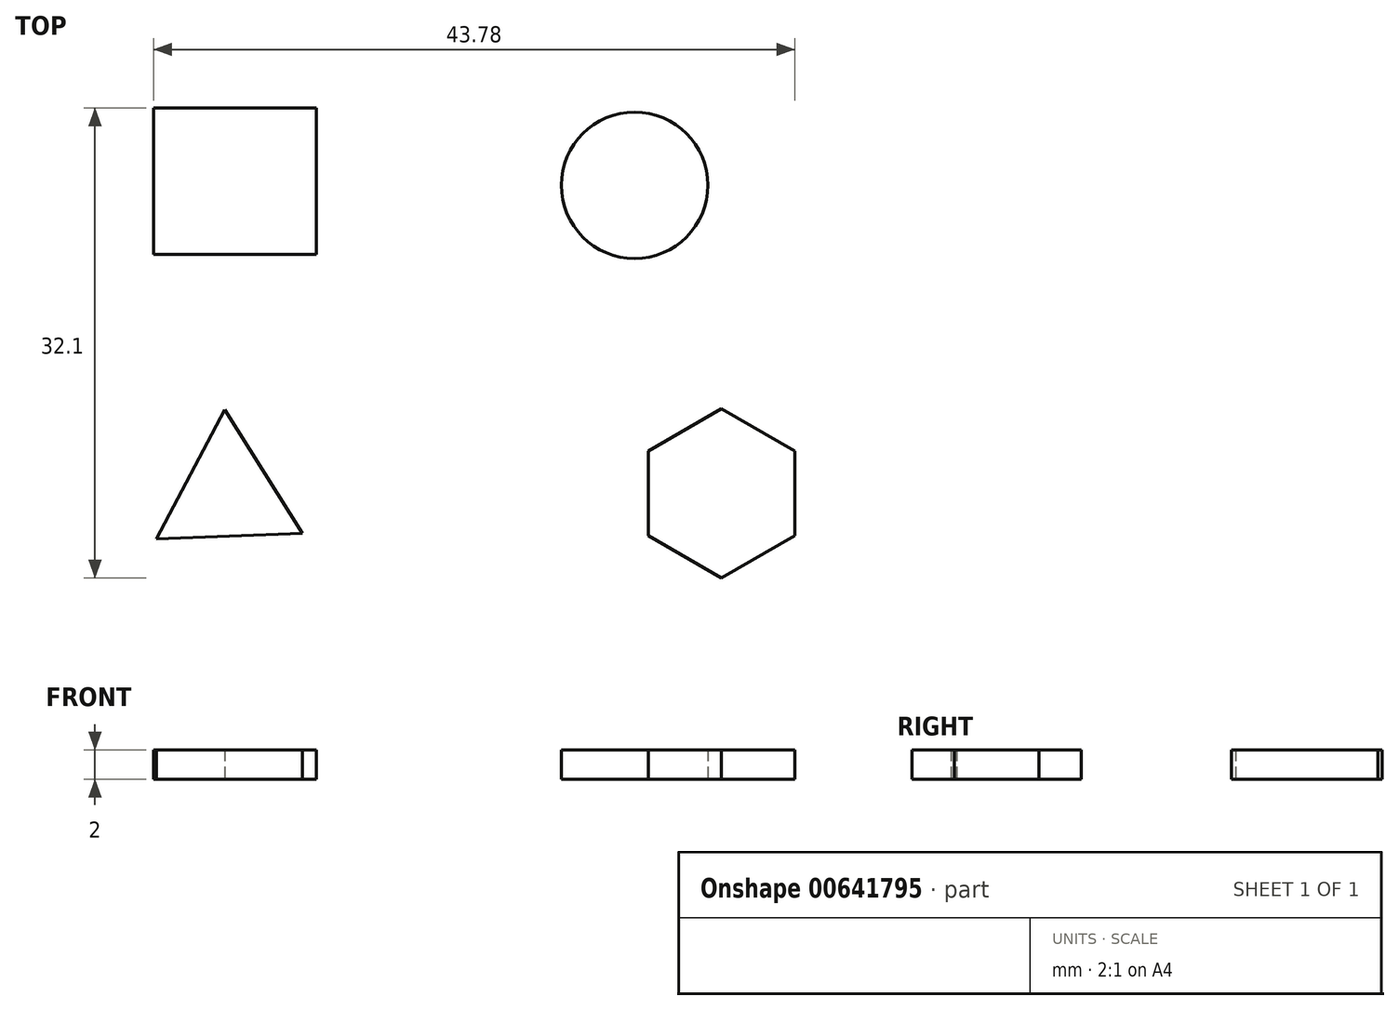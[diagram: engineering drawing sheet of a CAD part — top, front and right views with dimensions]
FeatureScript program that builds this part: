
annotation { "Feature Type Name" : "Feature", "Feature Type Description" : "" }
export const myFeature = defineFeature(function(context is Context, id is Id, definition is map)
    precondition{}
    {
        {
            var Q0;
            Q0=qCreatedBy(makeId("Top.planeOp"),FACE);
            var sketch = newSketch(context, id + "F0", { "sketchPlane" : qUnion([Q0])});
            skCircle(sketch, "E0", {"center": v(7.96, 9.92) * mm, "radius": 5 * mm});
            skLineSegment(sketch, "E1.bottom", {"start": v(-13.78, 15.2) * mm, "end": v(-24.88, 15.2) * mm});
            skLineSegment(sketch, "E1.top", {"start": v(-13.78, 5.2) * mm, "end": v(-24.88, 5.2) * mm});
            skLineSegment(sketch, "E1.left", {"start": v(-13.78, 15.2) * mm, "end": v(-13.78, 5.2) * mm});
            skLineSegment(sketch, "E1.right", {"start": v(-24.88, 15.2) * mm, "end": v(-24.88, 5.2) * mm});
            skPoint(sketch, "E1.middle", {"position": v(-19.33, 10.2) * mm});
            skLineSegment(sketch, "E2", {"start": v(-24.7, -14.23) * mm, "end": v(-20.02, -5.4) * mm});
            skLineSegment(sketch, "E3", {"start": v(-20.02, -5.4) * mm, "end": v(-14.7, -13.86) * mm});
            skLineSegment(sketch, "E4", {"start": v(-14.7, -13.86) * mm, "end": v(-24.7, -14.23) * mm});
            skCircle(sketch, "E5.cCircle", {"center": v(13.9, -11.13) * mm, "radius": 5 * mm, "construction": true});
            skLineSegment(sketch, "E5.0", {"start": v(18.9, -8.24) * mm, "end": v(18.9, -14.01) * mm});
            skLineSegment(sketch, "E5.1", {"start": v(18.9, -14.01) * mm, "end": v(13.9, -16.9) * mm});
            skLineSegment(sketch, "E5.2", {"start": v(13.9, -16.9) * mm, "end": v(8.9, -14.01) * mm});
            skLineSegment(sketch, "E5.3", {"start": v(8.9, -14.01) * mm, "end": v(8.9, -8.24) * mm});
            skLineSegment(sketch, "E5.4", {"start": v(8.9, -8.24) * mm, "end": v(13.9, -5.35) * mm});
            skLineSegment(sketch, "E5.5", {"start": v(13.9, -5.35) * mm, "end": v(18.9, -8.24) * mm});
            skPoint(sketch, "E5.0.midPoint", {"position": v(18.9, -11.13) * mm});
            skSolve(sketch);
        }
        {
            var Q0;
            Q0=makeQuery(id+"F0.imprint","IMPRINT",FACE,{"disambiguationData":[TD([[makeQuery(id+"F0.imprint","IMPRINT",EDGE,{"derivedFrom":sQuery(id+"F0.wireOp",EDGE,"E2")}),-1.0]])]});
            var Q1;
            Q1=makeQuery(id+"F0.imprint","IMPRINT",FACE,{"disambiguationData":[TD([[makeQuery(id+"F0.imprint","IMPRINT",EDGE,{"derivedFrom":sQuery(id+"F0.wireOp",EDGE,"E1.bottom")}),1.0]])]});
            var Q2;
            Q2=makeQuery(id+"F0.imprint","IMPRINT",FACE,{"disambiguationData":[TD([[makeQuery(id+"F0.imprint","IMPRINT",EDGE,{"derivedFrom":sQuery(id+"F0.wireOp",EDGE,"E0")}),1.0]])]});
            var Q3;
            Q3=makeQuery(id+"F0.imprint","IMPRINT",FACE,{"disambiguationData":[TD([[makeQuery(id+"F0.imprint","IMPRINT",EDGE,{"derivedFrom":sQuery(id+"F0.wireOp",EDGE,"E5.0")}),-1.0]])]});
            extrude(context, id + "F1", {"entities" : qUnion([Q0, Q1, Q2, Q3]), "depth" : 2 * mm, "offsetDistance" : 25 * mm});
        }
    });
